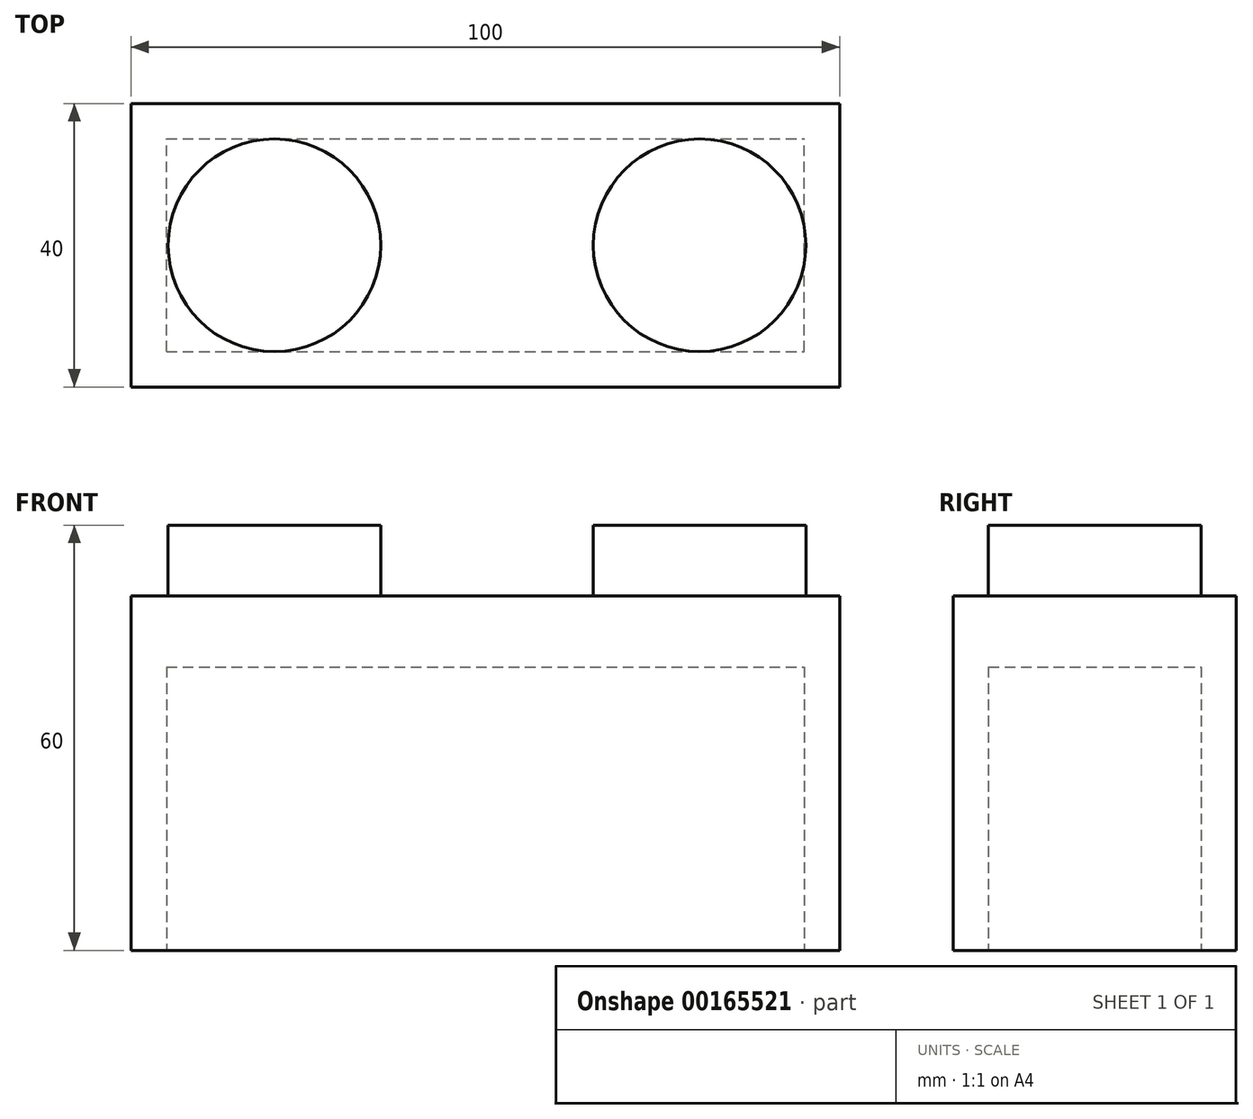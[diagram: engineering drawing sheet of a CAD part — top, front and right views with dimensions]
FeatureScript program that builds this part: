
annotation { "Feature Type Name" : "Feature", "Feature Type Description" : "" }
export const myFeature = defineFeature(function(context is Context, id is Id, definition is map)
    precondition{}
    {
        {
            var Q0;
            Q0=qCreatedBy(makeId("Front.planeOp"),FACE);
            var sketch = newSketch(context, id + "F0", { "sketchPlane" : qUnion([Q0])});
            skLineSegment(sketch, "E0.bottom", {"start": v(50, -25) * mm, "end": v(-50, -25) * mm});
            skLineSegment(sketch, "E0.top", {"start": v(50, 25) * mm, "end": v(-50, 25) * mm});
            skLineSegment(sketch, "E0.left", {"start": v(50, -25) * mm, "end": v(50, 25) * mm});
            skLineSegment(sketch, "E0.right", {"start": v(-50, -25) * mm, "end": v(-50, 25) * mm});
            skPoint(sketch, "E0.middle", {"position": v(0, 0) * mm});
            skSolve(sketch);
        }
        {
            var Q0;
            Q0=makeQuery(id+"F0.imprint","IMPRINT",FACE,{"disambiguationData":[TD([[makeQuery(id+"F0.imprint","IMPRINT",EDGE,{"derivedFrom":sQuery(id+"F0.wireOp",EDGE,"E0.bottom")}),-1.0]])]});
            extrude(context, id + "F1", {"entities" : qUnion([Q0]), "depth" : 40 * mm});
        }
        {
            var Q0;
            Q0=makeQuery(id+"F1.opExtrude","SWEPT_FACE",FACE,{"disambiguationData":[OSD([sQuery(id+"F0.wireOp",EDGE,"E0.top")])]});
            var sketch = newSketch(context, id + "F2", { "sketchPlane" : qUnion([Q0])});
            skCircle(sketch, "E1", {"center": v(-29.76, -20) * mm, "radius": 15 * mm});
            skPoint(sketch, "E1.centerSnap0", {"position": v(-50, -20) * mm});
            skCircle(sketch, "E2", {"center": v(30.24, -20) * mm, "radius": 15 * mm});
            skPoint(sketch, "E2.centerSnap0", {"position": v(50, -20) * mm});
            skSolve(sketch);
        }
        {
            var Q0;
            Q0=qSketchRegion(id+"F2",true);
            extrude(context, id + "F3", {"entities" : qUnion([Q0]), "operationType" : NewBodyOperationType.ADD, "depth" : 10 * mm});
        }
        {
            var Q0;
            Q0=makeQuery(id+"F1.opExtrude","SWEPT_FACE",FACE,{"disambiguationData":[OSD([sQuery(id+"F0.wireOp",EDGE,"E0.bottom")])]});
            var sketch = newSketch(context, id + "F4", { "sketchPlane" : qUnion([Q0])});
            skLineSegment(sketch, "E3.bottom", {"start": v(-50, 40) * mm, "end": v(50, 40) * mm});
            skLineSegment(sketch, "E3.top", {"start": v(-50, 0) * mm, "end": v(50, 0) * mm});
            skLineSegment(sketch, "E3.left", {"start": v(-50, 40) * mm, "end": v(-50, 0) * mm});
            skLineSegment(sketch, "E3.right", {"start": v(50, 40) * mm, "end": v(50, 0) * mm});
            skSolve(sketch);
        }
        {
            var Q0;
            Q0=makeQuery(id+"F4.imprint","IMPRINT",FACE,{"disambiguationData":[TD([[makeQuery(id+"F4.imprint","IMPRINT",EDGE,{"derivedFrom":sQuery(id+"F4.wireOp",EDGE,"E3.bottom")}),1.0]])]});
            var sketch = newSketch(context, id + "F5", { "sketchPlane" : qUnion([Q0])});
            skLineSegment(sketch, "E4.bottom", {"start": v(-45, 35) * mm, "end": v(45, 35) * mm});
            skLineSegment(sketch, "E4.top", {"start": v(-45, 5) * mm, "end": v(45, 5) * mm});
            skLineSegment(sketch, "E4.left", {"start": v(-45, 35) * mm, "end": v(-45, 5) * mm});
            skLineSegment(sketch, "E4.right", {"start": v(45, 35) * mm, "end": v(45, 5) * mm});
            skSolve(sketch);
        }
        {
            var Q0;
            Q0=qSketchRegion(id+"F5",true);
            extrude(context, id + "F6", {"entities" : qUnion([Q0]), "operationType" : NewBodyOperationType.REMOVE, "oppositeDirection" : true, "depth" : 40 * mm});
        }
    });
